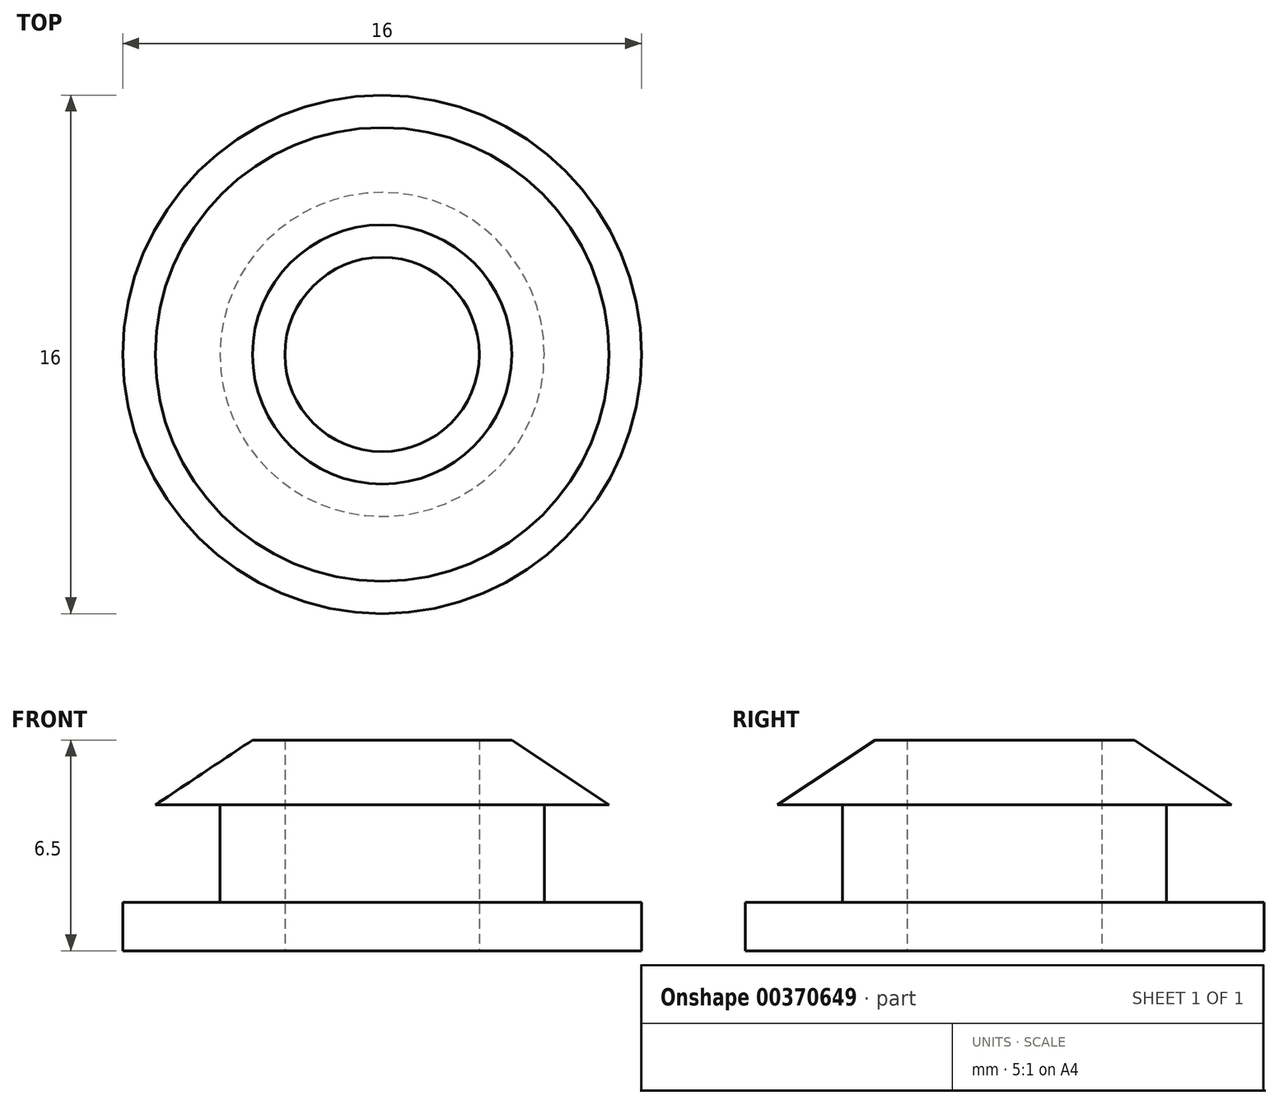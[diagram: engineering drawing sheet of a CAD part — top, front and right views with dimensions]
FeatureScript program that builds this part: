
annotation { "Feature Type Name" : "Feature", "Feature Type Description" : "" }
export const myFeature = defineFeature(function(context is Context, id is Id, definition is map)
    precondition{}
    {
        {
            var Q0;
            Q0=qCreatedBy(makeId("Front.planeOp"),FACE);
            var sketch = newSketch(context, id + "F0", { "sketchPlane" : qUnion([Q0])});
            skLineSegment(sketch, "E0", {"start": v(-3, 6.5) * mm, "end": v(-4, 6.5) * mm});
            skLineSegment(sketch, "E1", {"start": v(-4, 6.5) * mm, "end": v(-7, 4.5) * mm});
            skLineSegment(sketch, "E2", {"start": v(-7, 4.5) * mm, "end": v(-5, 4.5) * mm});
            skLineSegment(sketch, "E3", {"start": v(-5, 4.5) * mm, "end": v(-5, 1.5) * mm});
            skLineSegment(sketch, "E4", {"start": v(-5, 1.5) * mm, "end": v(-8, 1.5) * mm});
            skLineSegment(sketch, "E5", {"start": v(-8, 1.5) * mm, "end": v(-8, 0) * mm});
            skLineSegment(sketch, "E6", {"start": v(-8, 0) * mm, "end": v(-3, 0) * mm});
            skLineSegment(sketch, "E7", {"start": v(-3, 0) * mm, "end": v(-3, 6.5) * mm});
            skLineSegment(sketch, "E8", {"start": v(0, -15.71) * mm, "end": v(0, 21.33) * mm});
            skSolve(sketch);
        }
        {
            var Q0;
            Q0=qSketchRegion(id+"F0",true);
            var Q1;
            Q1=sQuery(id+"F0.wireOp",EDGE,"E8");
            revolve(context, id + "F1", {"entities" : qUnion([Q0]), "axis" : qUnion([Q1]), "revolveType" : RevolveType.FULL});
        }
    });
